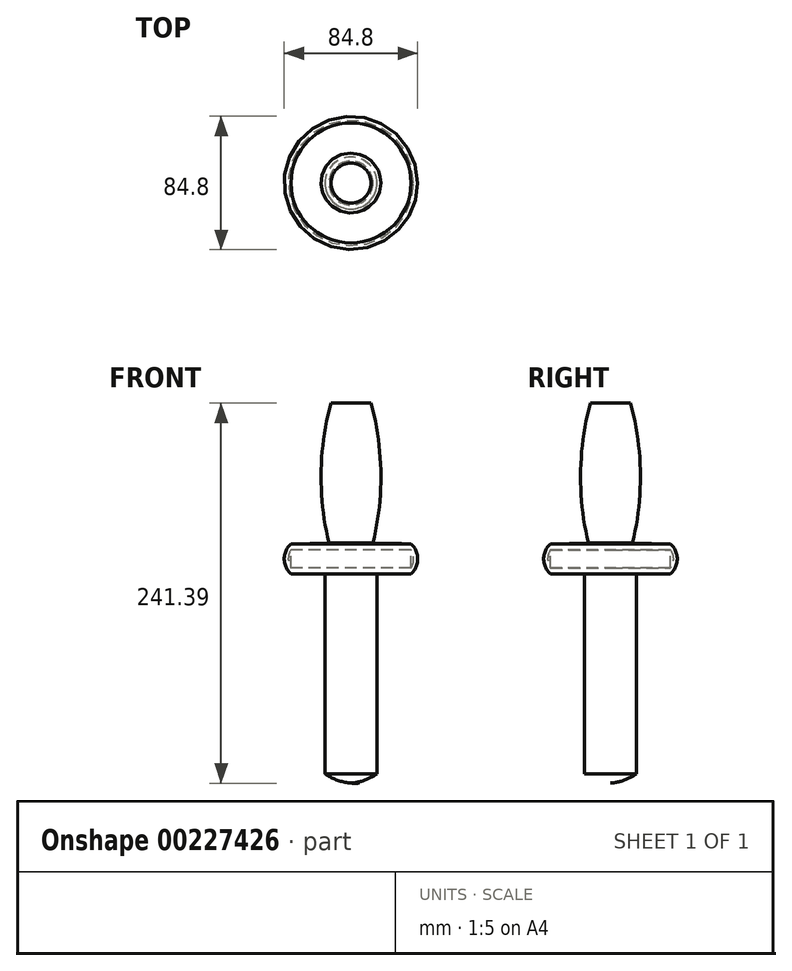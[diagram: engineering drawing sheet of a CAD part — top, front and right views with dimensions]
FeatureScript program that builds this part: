
annotation { "Feature Type Name" : "Feature", "Feature Type Description" : "" }
export const myFeature = defineFeature(function(context is Context, id is Id, definition is map)
    precondition{}
    {
        {
            var Q0;
            Q0=qCreatedBy(makeId("Front.planeOp"),FACE);
            var sketch = newSketch(context, id + "F0", { "sketchPlane" : qUnion([Q0])});
            skArc(sketch, "E0", {"start": v(13.97, 76.33) * mm, "mid": v(18.98, 120.86) * mm, "end": v(12.7, 165.23) * mm});
            skLineSegment(sketch, "E1", {"start": v(16.51, -70.13) * mm, "end": v(16.51, 56.87) * mm});
            skLineSegment(sketch, "E2", {"start": v(16.51, 56.87) * mm, "end": v(38.1, 56.87) * mm});
            skLineSegment(sketch, "E3", {"start": v(38.1, 56.87) * mm, "end": v(38.1, 75.92) * mm});
            skLineSegment(sketch, "E4", {"start": v(38.1, 75.92) * mm, "end": v(13.97, 76.33) * mm});
            skArc(sketch, "E5", {"start": v(38.1, 56.87) * mm, "mid": v(42.4, 66.4) * mm, "end": v(38.1, 75.92) * mm});
            skLineSegment(sketch, "E6", {"start": v(0, 165.23) * mm, "end": v(12.7, 165.23) * mm});
            skArc(sketch, "E7", {"start": v(0, -76.07) * mm, "mid": v(8.66, -74.22) * mm, "end": v(16.51, -70.13) * mm});
            skArc(sketch, "E8.0", {"start": v(0, -73.52) * mm, "mid": v(7.28, -72) * mm, "end": v(13.97, -68.78) * mm});
            skLineSegment(sketch, "E8.1", {"start": v(13.97, -68.78) * mm, "end": v(13.97, 59.4) * mm});
            skLineSegment(sketch, "E8.2", {"start": v(13.97, 59.4) * mm, "end": v(37.08, 59.4) * mm});
            skLineSegment(sketch, "E8.3", {"start": v(0, 162.7) * mm, "end": v(10.75, 162.7) * mm});
            skArc(sketch, "E8.4", {"start": v(10.72, 73.85) * mm, "mid": v(16.46, 118.27) * mm, "end": v(10.75, 162.7) * mm});
            skLineSegment(sketch, "E8.5", {"start": v(37.06, 73.4) * mm, "end": v(10.72, 73.85) * mm});
            skArc(sketch, "E8.6", {"start": v(37.08, 59.4) * mm, "mid": v(39.86, 66.4) * mm, "end": v(37.06, 73.4) * mm});
            skLineSegment(sketch, "E9", {"start": v(0, -76.07) * mm, "end": v(0, -73.52) * mm});
            skLineSegment(sketch, "E10", {"start": v(0, 165.23) * mm, "end": v(0, 162.7) * mm});
            skLineSegment(sketch, "E11", {"start": v(0, 0) * mm, "end": v(0, 50.03) * mm});
            skLineSegment(sketch, "E12", {"start": v(0, 165.23) * mm, "end": v(0, -76.07) * mm});
            skSolve(sketch);
        }
        {
            var Q0;
            {var subQ4=sQuery(id+"F0.wireOp",EDGE,"E8.0");Q0=makeQuery(id+"F0.imprint","IMPRINT",FACE,{"disambiguationData":[TD([[makeQuery(id+"F0.imprint","IMPRINT",EDGE,{"derivedFrom":subQ4}),1.0]])]});}
            var Q1;
            Q1=makeQuery(id+"F0.imprint","IMPRINT",FACE,{"disambiguationData":[TD([[makeQuery(id+"F0.imprint","IMPRINT",EDGE,{"derivedFrom":sQuery(id+"F0.wireOp",EDGE,"E0")}),1.0]])]});
            var Q2;
            {var subQ0=sQuery(id+"F0.wireOp",EDGE,"E5");Q2=makeQuery(id+"F0.imprint","IMPRINT",FACE,{"disambiguationData":[TD([[makeQuery(id+"F0.imprint","IMPRINT",EDGE,{"derivedFrom":subQ0}),1.0]])]});}
            var Q3;
            Q3=makeQuery(id+"F0.imprint","IMPRINT",FACE,{"disambiguationData":[TD([[makeQuery(id+"F0.imprint","IMPRINT",EDGE,{"derivedFrom":sQuery(id+"F0.wireOp",EDGE,"E1")}),1.0]])]});
            var Q4;
            Q4=sQuery(id+"F0.wireOp",EDGE,"E12");
            revolve(context, id + "F1", {"entities" : qUnion([Q0, Q1, Q2, Q3]), "axis" : qUnion([Q4]), "revolveType" : RevolveType.FULL});
        }
    });
